# Revit family: 19.Воздушная завеса с электрическим подогревом PWZ на базе вентилятора WRP
name_source: partatom
category: Оборудование
revit_build: Autodesk Revit 2016 (Build: 20161004_0715(x64)
units: mm (PartAtom-declared; Revit-internal decimal feet)

## family parameters
Всегда вертикально = Да
На основе рабочей плоскости = Нет
Общий = Нет
При загрузке вырезать с полостями = Нет
Размер круглого соединителя = Использовать диаметр
Тип детали = Нормальный
Точка расчета площади = Нет

## types (6) — shared parameters
Единица измерения = шт.
Завод изготовитель = KORF
И1 = 2000 мм
Ключевая пометка = Вентиляция
Материал = Сталь серая
Наименование и тех.хар-ка = Воздушная завеса с электрическим подогревом
Напряжение U,В = 3-380
Раздел = ОВ
Ширина щели = 42 мм
отступ = 50 мм
х2 = 1000 мм

## per-type parameters (varying)
| type | D | d | z | А | Б | Б1 | Высота | И2 | Мощность двигателя N,Вт | Мощность, кВт | Сила тока J, А | Тип, марка, обозначение | Ток эл. нагревателя, А | Ширина | х | х1 |
| 60-30 | 300 мм | 225 мм | 179 мм | 600 мм | 300 мм | 90 мм | 300 мм | 1502 мм | 1100 | 15 Вт | 2.5 | PWZ 60-30 E | 22,6 | 600 мм | 1051 мм | 526 мм |
| 60-35 | 324 мм | 243 мм | 193 мм | 600 мм | 350 мм | 105 мм | 350 мм | 1622 мм | 1500 | 23 Вт | 3,45 | PWZ 60-35 E | 33.9 | 600 мм | 1135 мм | 568 мм |
| 70-40 M | 320 мм | 240 мм | 191 мм | 700 мм | 400 мм | 120 мм | 400 мм | 1602 мм | 1500 | 30 Вт | 3,45 | PWZ 70-40 M E | 45.1 | 700 мм | 1121 мм | 561 мм |
| 70-40 | 320 мм | 240 мм | 191 мм | 700 мм | 400 мм | 120 мм | 400 мм | 1602 мм | 3 | 30 Вт | 5.9 | PWZ 70-40 E | 45.1 | 700 мм | 1121 мм | 561 мм |
| 80-50 | 345 мм | 259 мм | 206 мм | 800 мм | 500 мм | 150 мм | 500 мм | 1727 мм | 3000 | 30 Вт | 5.9 | PWZ 80-50 E | 45.1 | 800 мм | 1209 мм | 604 мм |
| 90-50 | 401 мм | 300 мм | 238 мм | 900 мм | 500 мм | 150 мм | 500 мм | 2003 мм | 5500 | 45 Вт | 10.7 | PWZ 90-50 E | 67.6 | 900 мм | 1402 мм | 701 мм |
